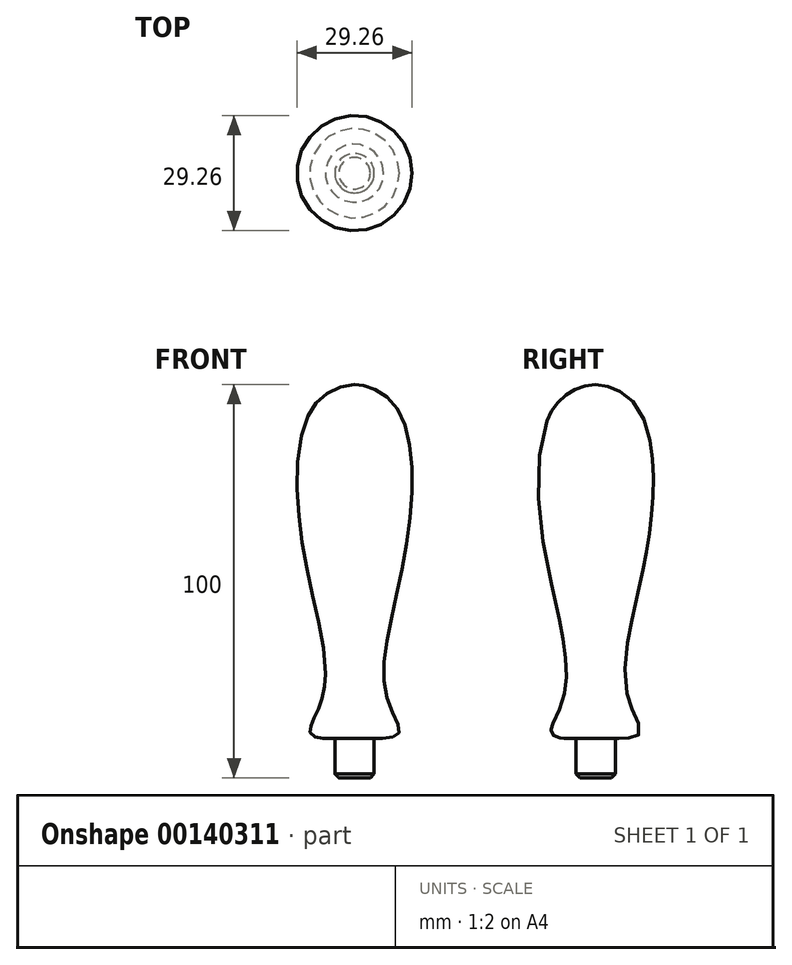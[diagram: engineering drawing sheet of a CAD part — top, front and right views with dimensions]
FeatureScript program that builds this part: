
annotation { "Feature Type Name" : "Feature", "Feature Type Description" : "" }
export const myFeature = defineFeature(function(context is Context, id is Id, definition is map)
    precondition{}
    {
        {
            var Q0;
            Q0=qCreatedBy(makeId("Front.planeOp"),FACE);
            var sketch = newSketch(context, id + "F0", { "sketchPlane" : qUnion([Q0])});
            skLineSegment(sketch, "E0", {"start": v(0, 0) * mm, "end": v(5, 0) * mm});
            skLineSegment(sketch, "E1", {"start": v(5, 0) * mm, "end": v(5, 10) * mm});
            skLineSegment(sketch, "E2", {"start": v(0, 0) * mm, "end": v(0, 100) * mm});
            skFitSpline(sketch, "E3", {"points": [v(0, 100) * mm, v(10, 95) * mm, v(13, 58) * mm, v(8, 21) * mm, v(11, 11) * mm, v(5, 10) * mm], "startDerivative": vector(39.9, 0) * mm, "endDerivative": vector(-28.97, 0.03) * mm});
            skSolve(sketch);
        }
        {
            var Q0;
            Q0=makeQuery(id+"F0.imprint","IMPRINT",FACE,{"disambiguationData":[TD([[makeQuery(id+"F0.imprint","IMPRINT",EDGE,{"derivedFrom":sQuery(id+"F0.wireOp",EDGE,"E0")}),1.0]])]});
            var Q1;
            Q1=sQuery(id+"F0.wireOp",EDGE,"E2");
            revolve(context, id + "F1", {"entities" : qUnion([Q0]), "axis" : qUnion([Q1]), "revolveType" : RevolveType.FULL});
        }
        {
            var Q0;
            Q0=makeQuery(id+"F1.opRevolve","SWEPT_EDGE",EDGE,{"disambiguationData":[OSD([sQuery(id+"F0.wireOp",EDGE,"E0"),sQuery(id+"F0.wireOp",EDGE,"E1")])]});
            chamfer(context, id + "F2", {"entities" : qUnion([Q0]), "width" : 1 * mm, "tangentPropagation" : true});
        }
    });
